# Revit family: Mailboxes_4C-Salsbury_Industries-Free_Standing-15_Door_High_Units
name_source: partatom
category: Specialty Equipment
revit_build: Autodesk Revit 2016 (Build: 20150714_1515(x64)
units: mm (PartAtom-declared; Revit-internal decimal feet)

## family parameters
Always vertical = Yes
Cut with Voids When Loaded = No
OmniClass Number = 23.40.90.14.11
OmniClass Title = Mail Boxes
Part Type = Normal
Room Calculation Point = No
Round Connector Dimension = Use Diameter
Shared = No
Work Plane-Based = No

## types (20) — shared parameters
4C Unit Elevation = 15.25 "
4C Unit Height = 55 "
Assembly Code = C1030910
Assembly Description = Mailboxes
Depth = 19 "
Front Panel Height = 14.254 "
Height = 72 "
Lock Material = Stainless Steel - Salsbury Finish -  Polished
Manufacturer = Salsbury Industries
MasterFormat Number = 10 55 00
MasterFormat Title = Postal Specialties
OmniClass 23 Number = 23.40.90.14.11
OmniClass 23 Title = Mail Boxes
Type Comments = Free-Standing 4C Horizontal Mailboxes - Front Loading
URL = www.mailboxes.com
Version = 1.0 (06/30/17)
Visible Door Number = Yes

## per-type parameters (varying)
| type | 4C Unit | Description | Model | Width |
| 3915D-20 | Mailboxes_4C-Salsbury_Industries-Front_Load-15_Door_High_Units : 3715S-09 FL | 15 Door High Unit:  9 MB1, 1 PL4, OM2 | 3915S-09 | 17.496 " |
| 3915S-09 | Mailboxes_4C-Salsbury_Industries-Front_Load-15_Door_High_Units : 3715S-09 FL | 15 Door High Unit:  9 MB1, 1 PL4, OM2 | 3915S-09 | 17.496 " |
| 3915D-29 | Mailboxes_4C-Salsbury_Industries-Front_Load-15_Door_High_Units : 3715D-29 FL | 15 Door High Unit:  29 MB1, CA | 3915D-29 | 32.25 " |
| 3915D-28 | Mailboxes_4C-Salsbury_Industries-Front_Load-15_Door_High_Units : 3715D-28 FL | 15 Door High Unit:  28 MB1, OM2 | 3915D-28 | 32.25 " |
| 3915D-13 | Mailboxes_4C-Salsbury_Industries-Front_Load-15_Door_High_Units : 3715D-13 FL | 15 Door High Unit:  11 MB2, 2 MB3, OM2 | 3915D-13 | 32.25 " |
| 3915D-19 | Mailboxes_4C-Salsbury_Industries-Front_Load-15_Door_High_Units : 3715D-19 FL | 15 Door High Unit:  19 MB1, 1 PL4, 1 PL5, OM2 | 3915D-19 | 32.25 " |
| 3915D-18 | Mailboxes_4C-Salsbury_Industries-Front_Load-15_Door_High_Units : 3715D-18 FL | 15 Door High Unit:  18 MB1, 2 PL5, OM2 | 3915D-18 | 32.25 " |
| 3915D-17 | Mailboxes_4C-Salsbury_Industries-Front_Load-15_Door_High_Units : 3715D-17 FL | 15 Door High Unit:  17 MB1, 1 PL5, 1 PL6, OM2 | 3915D-17 | 32.25 " |
| 3915D-16 | Mailboxes_4C-Salsbury_Industries-Front_Load-15_Door_High_Units : 3715D-16 FL | 15 Door High Unit:  16 MB1, 2 PL6, OM2 | 3915D-16 | 32.25 " |
| 3915D-15 | Mailboxes_4C-Salsbury_Industries-Front_Load-15_Door_High_Units : 3715D-15 FL | 15 Door High Unit:  15 MB1, 2 PL6, OM3 | 3915D-15 | 32.25 " |
| 3915D-09 | Mailboxes_4C-Salsbury_Industries-Front_Load-15_Door_High_Units : 3715D-09 FL | 15 Door High Unit:  9 MB2, 2 PL5, OM2 | 3915D-09 | 32.25 " |
| 3915S-08 | Mailboxes_4C-Salsbury_Industries-Front_Load-15_Door_High_Units : 3715S-08 FL | 15 Door High Unit:  8 MB1, 1 PL5, OM2 | 3915S-08 | 17.496 " |
| 3915S-07 | Mailboxes_4C-Salsbury_Industries-Front_Load-15_Door_High_Units : 3715S-07 FL | 15 Door High Unit:  7 MB1, 1 PL6, OM2 | 3915S-07 | 17.496 " |
| 3915S-06 | Mailboxes_4C-Salsbury_Industries-Front_Load-15_Door_High_Units : 3715S-06 FL | 15 Door High Unit:  6 MB1, 1 PL6, OM3 | 3915S-06 | 17.496 " |
| 3915S-04 | Mailboxes_4C-Salsbury_Industries-Front_Load-15_Door_High_Units : 3715S-04 FL | 15 Door High Unit:  4 MB2, 1 PL5, OM2 | 3915S-04 | 17.496 " |
| 3915S-3P | Mailboxes_4C-Salsbury_Industries-Front_Load-15_Door_High_Units : 3715S-3P FL | 15 Door High Unit:  3 PL5 | 3915S-3P | 17.496 " |
| 3915S-14 | Mailboxes_4C-Salsbury_Industries-Front_Load-15_Door_High_Units : 3715S-14 FL | 15 Door High Unit:  14 MB1, CA | 3915S-14 | 17.496 " |
| 3915S-13 | Mailboxes_4C-Salsbury_Industries-Front_Load-15_Door_High_Units : 3715S-13 FL | 15 Door High Unit:  13 MB1, OM2 | 3915S-13 | 17.496 " |
| 3915S-2B | Mailboxes_4C-Salsbury_Industries-Front_Load-15_Door_High_Units : 3715S-2B FL | 15 Door High Unit:  2 Receptacle Bins | 3915S-2B | 17.496 " |
| 3915S-1C | Mailboxes_4C-Salsbury_Industries-Front_Load-15_Door_High_Units : 3715S-1C FL | 15 Door High Unit:  1 Collection Box | 3915S-1C | 17.496 " |

## geometry (parser evidence)
native form markers: Blend x6, Extrusion x4, Sweep x16
no freeform markers — native parametric forms only
